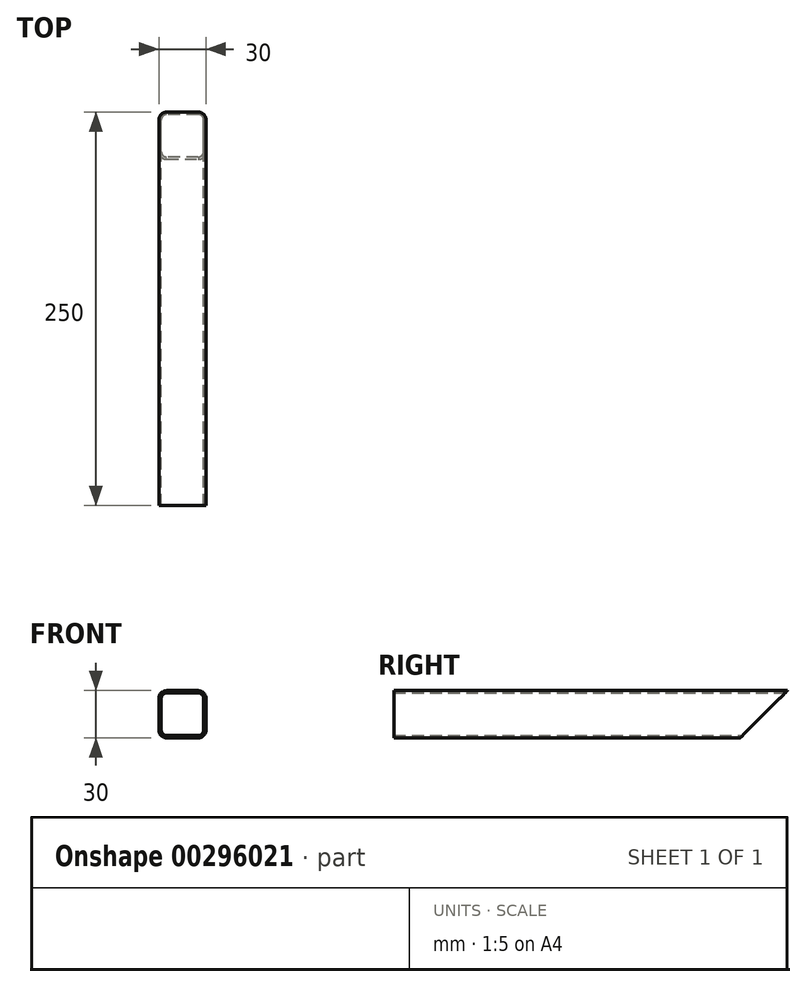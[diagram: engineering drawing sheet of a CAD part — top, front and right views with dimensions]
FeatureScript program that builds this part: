
annotation { "Feature Type Name" : "Feature", "Feature Type Description" : "" }
export const myFeature = defineFeature(function(context is Context, id is Id, definition is map)
    precondition{}
    {
        {
            var Q0;
            Q0=qCreatedBy(makeId("Front.planeOp"),FACE);
            var sketch = newSketch(context, id + "F0", { "sketchPlane" : qUnion([Q0])});
            skLineSegment(sketch, "E0.bottom", {"start": v(10, -15) * mm, "end": v(-10, -15) * mm});
            skLineSegment(sketch, "E0.top", {"start": v(10, 15) * mm, "end": v(-10, 15) * mm});
            skLineSegment(sketch, "E0.left", {"start": v(15, -10) * mm, "end": v(15, 10) * mm});
            skLineSegment(sketch, "E0.right", {"start": v(-15, -10) * mm, "end": v(-15, 10) * mm});
            skPoint(sketch, "E0.middle", {"position": v(0, 0) * mm});
            skPoint(sketch, "E1.visualSharp", {"position": v(-15, 15) * mm});
            skArc(sketch, "E1.filletArc", {"start": v(-10, 15) * mm, "mid": v(-13.54, 13.54) * mm, "end": v(-15, 10) * mm});
            skPoint(sketch, "E2.visualSharp", {"position": v(15, 15) * mm});
            skArc(sketch, "E2.filletArc", {"start": v(15, 10) * mm, "mid": v(13.54, 13.54) * mm, "end": v(10, 15) * mm});
            skPoint(sketch, "E3.visualSharp", {"position": v(15, -15) * mm});
            skArc(sketch, "E3.filletArc", {"start": v(10, -15) * mm, "mid": v(13.54, -13.54) * mm, "end": v(15, -10) * mm});
            skPoint(sketch, "E4.visualSharp", {"position": v(-15, -15) * mm});
            skArc(sketch, "E4.filletArc", {"start": v(-15, -10) * mm, "mid": v(-13.54, -13.54) * mm, "end": v(-10, -15) * mm});
            skLineSegment(sketch, "E5.0", {"start": v(-13.5, -10) * mm, "end": v(-13.5, 10) * mm});
            skLineSegment(sketch, "E5.1", {"start": v(10, -13.5) * mm, "end": v(-10, -13.5) * mm});
            skLineSegment(sketch, "E5.2", {"start": v(13.5, -10) * mm, "end": v(13.5, 10) * mm});
            skLineSegment(sketch, "E5.3", {"start": v(10, 13.5) * mm, "end": v(-10, 13.5) * mm});
            skPoint(sketch, "E6.visualSharp", {"position": v(-13.5, 13.5) * mm});
            skArc(sketch, "E6.filletArc", {"start": v(-10, 13.5) * mm, "mid": v(-12.47, 12.47) * mm, "end": v(-13.5, 10) * mm});
            skPoint(sketch, "E7.visualSharp", {"position": v(13.5, 13.5) * mm});
            skArc(sketch, "E7.filletArc", {"start": v(13.5, 10) * mm, "mid": v(12.47, 12.47) * mm, "end": v(10, 13.5) * mm});
            skPoint(sketch, "E8.visualSharp", {"position": v(13.5, -13.5) * mm});
            skArc(sketch, "E8.filletArc", {"start": v(10, -13.5) * mm, "mid": v(12.47, -12.47) * mm, "end": v(13.5, -10) * mm});
            skPoint(sketch, "E9.visualSharp", {"position": v(-13.5, -13.5) * mm});
            skArc(sketch, "E9.filletArc", {"start": v(-13.5, -10) * mm, "mid": v(-12.47, -12.47) * mm, "end": v(-10, -13.5) * mm});
            skSolve(sketch);
        }
        {
            var Q0;
            Q0=qSketchRegion(id+"F0",true);
            extrude(context, id + "F1", {"entities" : qUnion([Q0]), "depth" : 250 * mm});
        }
        {
            var Q0;
            Q0=makeQuery(id+"F1.opExtrude","SWEPT_FACE",FACE,{"disambiguationData":[OSD([sQuery(id+"F0.wireOp",EDGE,"E0.left")])]});
            var sketch = newSketch(context, id + "F2", { "sketchPlane" : qUnion([Q0])});
            skLineSegment(sketch, "E10", {"start": v(0, 15) * mm, "end": v(-30, -15) * mm});
            skLineSegment(sketch, "E11", {"start": v(-30, -15) * mm, "end": v(0, -15) * mm});
            skLineSegment(sketch, "E12", {"start": v(0, -15) * mm, "end": v(0, 15) * mm});
            skSolve(sketch);
        }
        {
            var Q0;
            Q0 = qSketchRegion(id + "F2", true);
            extrude(context, id + "F3", {"entities" : qUnion([Q0]), "operationType" : NewBodyOperationType.REMOVE, "endBound" : BoundingType.THROUGH_ALL, "oppositeDirection" : true, "depth" : 25 * mm});
        }
    });
